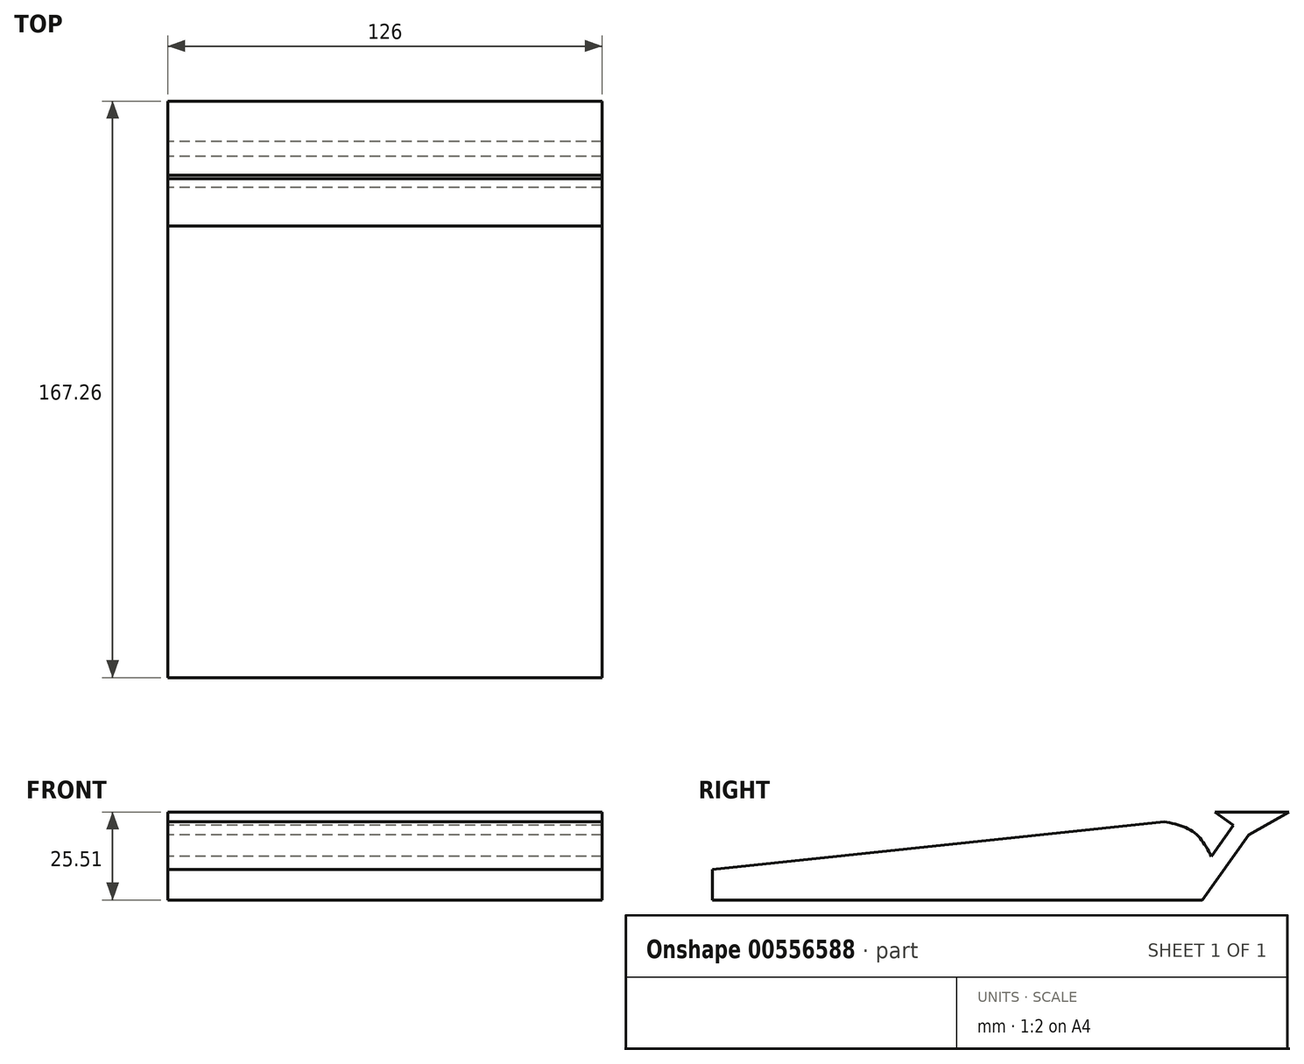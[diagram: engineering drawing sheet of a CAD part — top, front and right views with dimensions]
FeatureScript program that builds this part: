
annotation { "Feature Type Name" : "Feature", "Feature Type Description" : "" }
export const myFeature = defineFeature(function(context is Context, id is Id, definition is map)
    precondition{}
    {
        {
            var Q0;
            Q0=qCreatedBy(makeId("Right.planeOp"),FACE);
            var sketch = newSketch(context, id + "F0", { "sketchPlane" : qUnion([Q0])});
            skLineSegment(sketch, "E0", {"start": v(-74.15, 8.78) * mm, "end": v(56.87, 22.72) * mm});
            skLineSegment(sketch, "E1", {"start": v(-74.15, 8.78) * mm, "end": v(-74.15, 0) * mm});
            skLineSegment(sketch, "E2", {"start": v(-74.15, 0) * mm, "end": v(68.02, 0) * mm});
            skLineSegment(sketch, "E3", {"start": v(68.02, 0) * mm, "end": v(81.4, 18.82) * mm});
            skLineSegment(sketch, "E4", {"start": v(81.4, 18.82) * mm, "end": v(93.1, 25.5) * mm});
            skLineSegment(sketch, "E5", {"start": v(93.1, 25.5) * mm, "end": v(71.64, 25.5) * mm});
            skLineSegment(sketch, "E6", {"start": v(71.64, 25.5) * mm, "end": v(77.03, 21.67) * mm});
            skLineSegment(sketch, "E7", {"start": v(77.03, 21.67) * mm, "end": v(70.58, 12.6) * mm});
            skFitSpline(sketch, "E8", {"points": [v(56.87, 22.72) * mm, v(65.5, 19.65) * mm, v(70.58, 12.6) * mm], "startDerivative": vector(18.76, -3.96) * mm, "endDerivative": vector(8.62, -16.32) * mm});
            skSolve(sketch);
        }
        {
            var Q0;
            Q0=makeQuery(id+"F0.imprint","IMPRINT",FACE,{"disambiguationData":[TD([[makeQuery(id+"F0.imprint","IMPRINT",EDGE,{"derivedFrom":sQuery(id+"F0.wireOp",EDGE,"E0")}),-1.0]])]});
            extrude(context, id + "F1", {"entities" : qUnion([Q0]), "depth" : 126 * mm, "offsetDistance" : 25 * mm});
        }
    });
